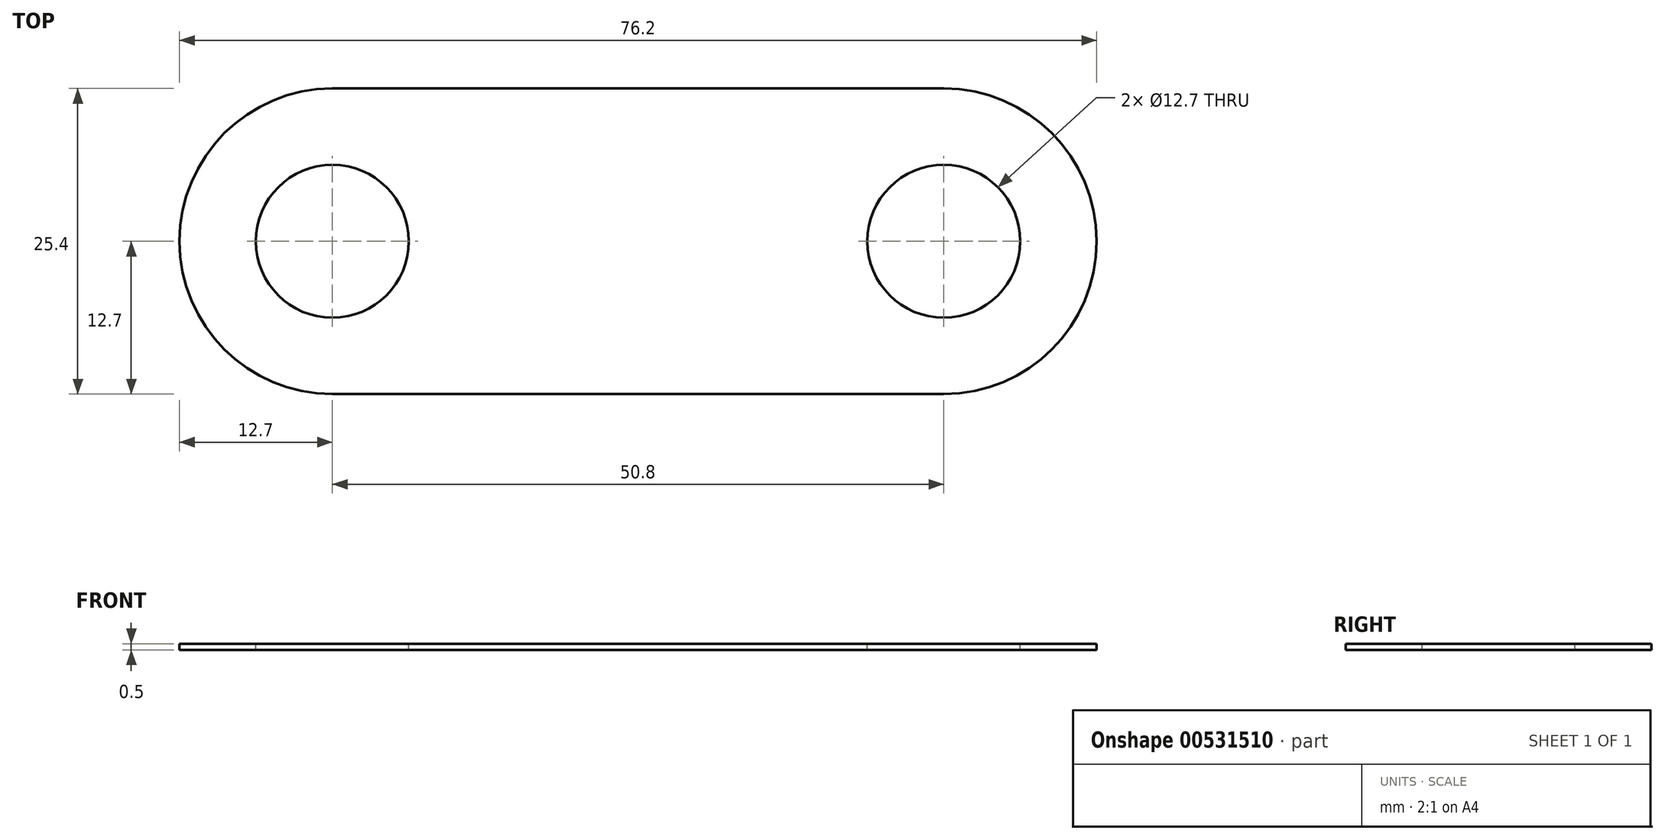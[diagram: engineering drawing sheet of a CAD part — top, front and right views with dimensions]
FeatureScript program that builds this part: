
annotation { "Feature Type Name" : "Feature", "Feature Type Description" : "" }
export const myFeature = defineFeature(function(context is Context, id is Id, definition is map)
    precondition{}
    {
        {
            assignVariable(context, id + "F0", {"name" : "w_link", "anyValue" : 1});
        }
        {
            var Q0;
            Q0=qCreatedBy(makeId("Top.planeOp"),FACE);
            var sketch = newSketch(context, id + "F1", { "sketchPlane" : qUnion([Q0])});
            skArc(sketch, "E0", {"start": v(0, -12.7) * mm, "mid": v(12.7, 0) * mm, "end": v(0, 12.7) * mm});
            skArc(sketch, "E1", {"start": v(-50.8, 12.7) * mm, "mid": v(-63.5, 0) * mm, "end": v(-50.8, -12.7) * mm});
            skLineSegment(sketch, "E2", {"start": v(-50.8, 12.7) * mm, "end": v(0, 12.7) * mm});
            skLineSegment(sketch, "E3", {"start": v(-71.47, 0) * mm, "end": v(26.62, 0) * mm, "construction": true});
            skLineSegment(sketch, "E4.MirrorCS", {"start": v(-50.8, -12.7) * mm, "end": v(0, -12.7) * mm});
            skSolve(sketch);
        }
        {
            var Q0;
            Q0 = qSketchRegion(id + "F1", true);
            extrude(context, id + "F2", {"entities" : qUnion([Q0]), "depth" : (getVariable(context, 'w_link') / 2) * mm, "offsetDistance" : 25.4 * mm});
        }
        {
            var Q0;
            Q0=makeQuery(id+"F2.opExtrude","CAP_FACE",FACE,{"disambiguationData":[OSD([sQuery(id+"F1.wireOp",EDGE,"E0"),sQuery(id+"F1.wireOp",EDGE,"E1"),sQuery(id+"F1.wireOp",EDGE,"E2"),sQuery(id+"F1.wireOp",EDGE,"E4.MirrorCS")])],"isStart":false});
            var sketch = newSketch(context, id + "F3", { "sketchPlane" : qUnion([Q0])});
            skCircle(sketch, "E5", {"center": v(0, 0) * mm, "radius": 6.35 * mm});
            skCircle(sketch, "E6", {"center": v(-50.8, 0) * mm, "radius": 6.35 * mm});
            skSolve(sketch);
        }
        {
            var Q0;
            Q0 = qSketchRegion(id + "F3", true);
            extrude(context, id + "F4", {"entities" : qUnion([Q0]), "operationType" : NewBodyOperationType.REMOVE, "endBound" : BoundingType.THROUGH_ALL, "oppositeDirection" : true, "depth" : 25.4 * mm, "offsetDistance" : 25.4 * mm});
        }
    });
